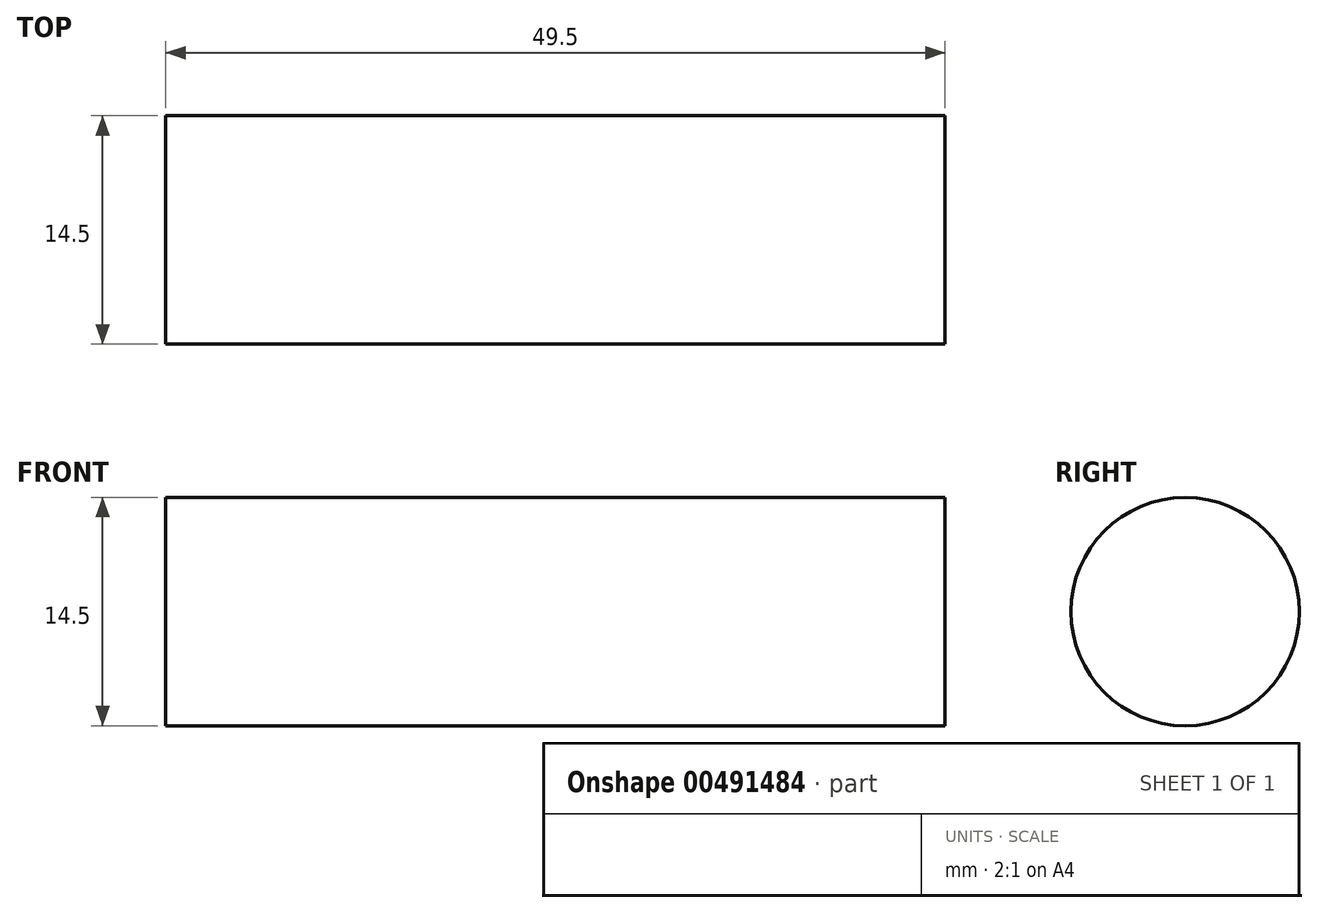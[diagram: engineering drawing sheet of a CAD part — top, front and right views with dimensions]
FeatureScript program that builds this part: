
annotation { "Feature Type Name" : "Feature", "Feature Type Description" : "" }
export const myFeature = defineFeature(function(context is Context, id is Id, definition is map)
    precondition{}
    {
        {
            var Q0;
            Q0=qCreatedBy(makeId("Right.planeOp"),FACE);
            var sketch = newSketch(context, id + "F0", { "sketchPlane" : qUnion([Q0])});
            skCircle(sketch, "E0", {"center": v(0, 0) * mm, "radius": 7.25 * mm});
            skSolve(sketch);
        }
        {
            var Q0;
            Q0=makeQuery(id+"F0.imprint","IMPRINT",FACE,{"disambiguationData":[TD([[makeQuery(id+"F0.imprint","IMPRINT",EDGE,{"derivedFrom":sQuery(id+"F0.wireOp",EDGE,"E0")}),1.0]])]});
            extrude(context, id + "F1", {"entities" : qUnion([Q0]), "oppositeDirection" : true, "depth" : 49.5 * mm});
        }
    });
